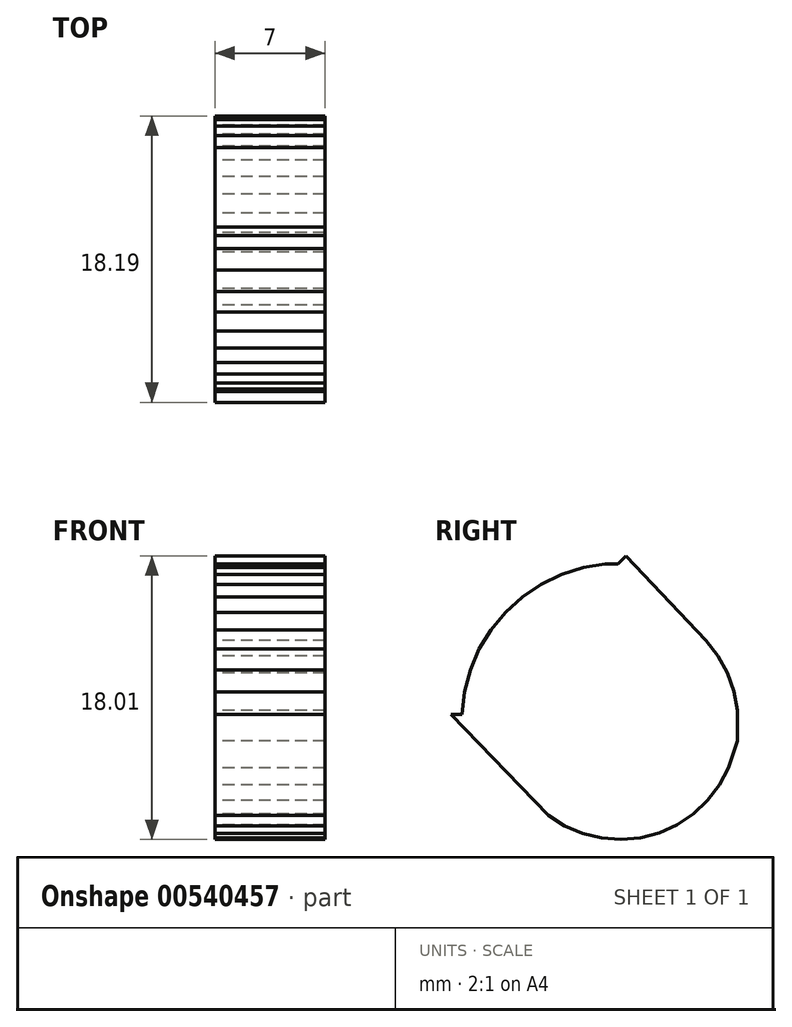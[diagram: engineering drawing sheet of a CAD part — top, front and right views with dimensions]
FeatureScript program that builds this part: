
annotation { "Feature Type Name" : "Feature", "Feature Type Description" : "" }
export const myFeature = defineFeature(function(context is Context, id is Id, definition is map)
    precondition{}
    {
        {
            var Q0;
            Q0=qCreatedBy(makeId("Right.planeOp"),FACE);
            var sketch = newSketch(context, id + "F0", { "sketchPlane" : qUnion([Q0])});
            skLineSegment(sketch, "E0", {"start": v(-4.1, -6.82) * mm, "end": v(-3.05, -7.49) * mm});
            skLineSegment(sketch, "E1", {"start": v(-0.7, -8.26) * mm, "end": v(0.53, -8.35) * mm});
            skLineSegment(sketch, "E2", {"start": v(0.53, -8.35) * mm, "end": v(1.76, -8.24) * mm});
            skLineSegment(sketch, "E3", {"start": v(1.76, -8.24) * mm, "end": v(2.96, -7.92) * mm});
            skLineSegment(sketch, "E4", {"start": v(2.96, -7.92) * mm, "end": v(4.1, -7.4) * mm});
            skLineSegment(sketch, "E5", {"start": v(4.1, -7.4) * mm, "end": v(5.12, -6.72) * mm});
            skLineSegment(sketch, "E6", {"start": v(5.12, -6.72) * mm, "end": v(6.02, -5.87) * mm});
            skLineSegment(sketch, "E7", {"start": v(6.02, -5.87) * mm, "end": v(6.77, -4.89) * mm});
            skLineSegment(sketch, "E8", {"start": v(6.77, -4.89) * mm, "end": v(7.35, -3.8) * mm});
            skLineSegment(sketch, "E9", {"start": v(7.35, -3.8) * mm, "end": v(7.74, -2.61) * mm});
            skLineSegment(sketch, "E10", {"start": v(-3.05, -7.49) * mm, "end": v(-1.9, -7.97) * mm});
            skLineSegment(sketch, "E11", {"start": v(-1.9, -7.97) * mm, "end": v(-0.7, -8.26) * mm});
            skLineSegment(sketch, "E12", {"start": v(7.74, -2.61) * mm, "end": v(7.92, -2.08) * mm});
            skLineSegment(sketch, "E13", {"start": v(7.92, -2.08) * mm, "end": v(7.92, -0.15) * mm});
            skLineSegment(sketch, "E14", {"start": v(7.92, -0.15) * mm, "end": v(7.7, 1.07) * mm});
            skLineSegment(sketch, "E15", {"start": v(7.7, 1.07) * mm, "end": v(7.29, 2.23) * mm});
            skLineSegment(sketch, "E16", {"start": v(7.29, 2.23) * mm, "end": v(6.68, 3.32) * mm});
            skLineSegment(sketch, "E17", {"start": v(6.68, 3.32) * mm, "end": v(5.91, 4.29) * mm});
            skLineSegment(sketch, "E18", {"start": v(5.91, 4.29) * mm, "end": v(0.86, 9.66) * mm});
            skLineSegment(sketch, "E19", {"start": v(0.34, 9.15) * mm, "end": v(-0.5, 9.15) * mm});
            skLineSegment(sketch, "E20", {"start": v(-0.5, 9.15) * mm, "end": v(-1.86, 8.92) * mm});
            skLineSegment(sketch, "E21", {"start": v(-1.86, 8.92) * mm, "end": v(-3.24, 8.48) * mm});
            skLineSegment(sketch, "E22", {"start": v(-3.24, 8.48) * mm, "end": v(-4.54, 7.86) * mm});
            skLineSegment(sketch, "E23", {"start": v(-4.54, 7.86) * mm, "end": v(-5.74, 7.05) * mm});
            skLineSegment(sketch, "E24", {"start": v(-5.74, 7.05) * mm, "end": v(-6.8, 6.08) * mm});
            skLineSegment(sketch, "E25", {"start": v(-6.8, 6.08) * mm, "end": v(-7.73, 4.97) * mm});
            skLineSegment(sketch, "E26", {"start": v(-7.73, 4.97) * mm, "end": v(-8.48, 3.74) * mm});
            skLineSegment(sketch, "E27", {"start": v(-8.48, 3.74) * mm, "end": v(-9.05, 2.4) * mm});
            skLineSegment(sketch, "E28", {"start": v(-9.05, 2.4) * mm, "end": v(-9.41, 1.01) * mm});
            skLineSegment(sketch, "E29", {"start": v(-9.41, 1.01) * mm, "end": v(-9.58, -0.42) * mm});
            skLineSegment(sketch, "E30", {"start": v(0.34, 9.15) * mm, "end": v(0.86, 9.66) * mm});
            skLineSegment(sketch, "E31", {"start": v(-9.58, -0.42) * mm, "end": v(-10.27, -0.4) * mm});
            skLineSegment(sketch, "E32", {"start": v(-10.27, -0.4) * mm, "end": v(-4.1, -6.82) * mm});
            skSolve(sketch);
        }
        {
            var Q0;
            Q0=makeQuery(id+"F0.imprint","IMPRINT",FACE,{"disambiguationData":[TD([[makeQuery(id+"F0.imprint","IMPRINT",EDGE,{"derivedFrom":sQuery(id+"F0.wireOp",EDGE,"E0")}),1.0]])]});
            var Q1;
            Q1=sQuery(id+"F0.wireOp",EDGE,"E0");
            var Q2;
            Q2=sQuery(id+"F0.wireOp",EDGE,"E1");
            var Q3;
            Q3=sQuery(id+"F0.wireOp",EDGE,"E2");
            var Q4;
            Q4=sQuery(id+"F0.wireOp",EDGE,"E3");
            var Q5;
            Q5=sQuery(id+"F0.wireOp",EDGE,"E4");
            var Q6;
            Q6=sQuery(id+"F0.wireOp",EDGE,"E5");
            var Q7;
            Q7=sQuery(id+"F0.wireOp",EDGE,"E6");
            var Q8;
            Q8=sQuery(id+"F0.wireOp",EDGE,"E7");
            var Q9;
            Q9=sQuery(id+"F0.wireOp",EDGE,"E8");
            var Q10;
            Q10=sQuery(id+"F0.wireOp",EDGE,"E9");
            var Q11;
            Q11=sQuery(id+"F0.wireOp",EDGE,"E10");
            var Q12;
            Q12=sQuery(id+"F0.wireOp",EDGE,"E11");
            var Q13;
            Q13=sQuery(id+"F0.wireOp",EDGE,"E12");
            var Q14;
            Q14=sQuery(id+"F0.wireOp",EDGE,"E13");
            var Q15;
            Q15=sQuery(id+"F0.wireOp",EDGE,"E14");
            var Q16;
            Q16=sQuery(id+"F0.wireOp",EDGE,"E15");
            var Q17;
            Q17=sQuery(id+"F0.wireOp",EDGE,"E16");
            var Q18;
            Q18=sQuery(id+"F0.wireOp",EDGE,"E17");
            var Q19;
            Q19=sQuery(id+"F0.wireOp",EDGE,"E18");
            var Q20;
            Q20=sQuery(id+"F0.wireOp",EDGE,"E19");
            var Q21;
            Q21=sQuery(id+"F0.wireOp",EDGE,"E20");
            var Q22;
            Q22=sQuery(id+"F0.wireOp",EDGE,"E21");
            var Q23;
            Q23=sQuery(id+"F0.wireOp",EDGE,"E22");
            var Q24;
            Q24=sQuery(id+"F0.wireOp",EDGE,"E23");
            var Q25;
            Q25=sQuery(id+"F0.wireOp",EDGE,"E24");
            var Q26;
            Q26=sQuery(id+"F0.wireOp",EDGE,"E25");
            var Q27;
            Q27=sQuery(id+"F0.wireOp",EDGE,"E26");
            var Q28;
            Q28=sQuery(id+"F0.wireOp",EDGE,"E27");
            var Q29;
            Q29=sQuery(id+"F0.wireOp",EDGE,"E28");
            var Q30;
            Q30=sQuery(id+"F0.wireOp",EDGE,"E29");
            var Q31;
            Q31=sQuery(id+"F0.wireOp",EDGE,"E30");
            var Q32;
            Q32=sQuery(id+"F0.wireOp",EDGE,"E31");
            var Q33;
            Q33=sQuery(id+"F0.wireOp",EDGE,"E32");
            extrude(context, id + "F1", {"entities" : qUnion([Q0]), "surfaceEntities" : qUnion([Q1, Q2, Q3, Q4, Q5, Q6, Q7, Q8, Q9, Q10, Q11, Q12, Q13, Q14, Q15, Q16, Q17, Q18, Q19, Q20, Q21, Q22, Q23, Q24, Q25, Q26, Q27, Q28, Q29, Q30, Q31, Q32, Q33]), "depth" : 7 * mm, "offsetDistance" : 25 * mm});
        }
    });
